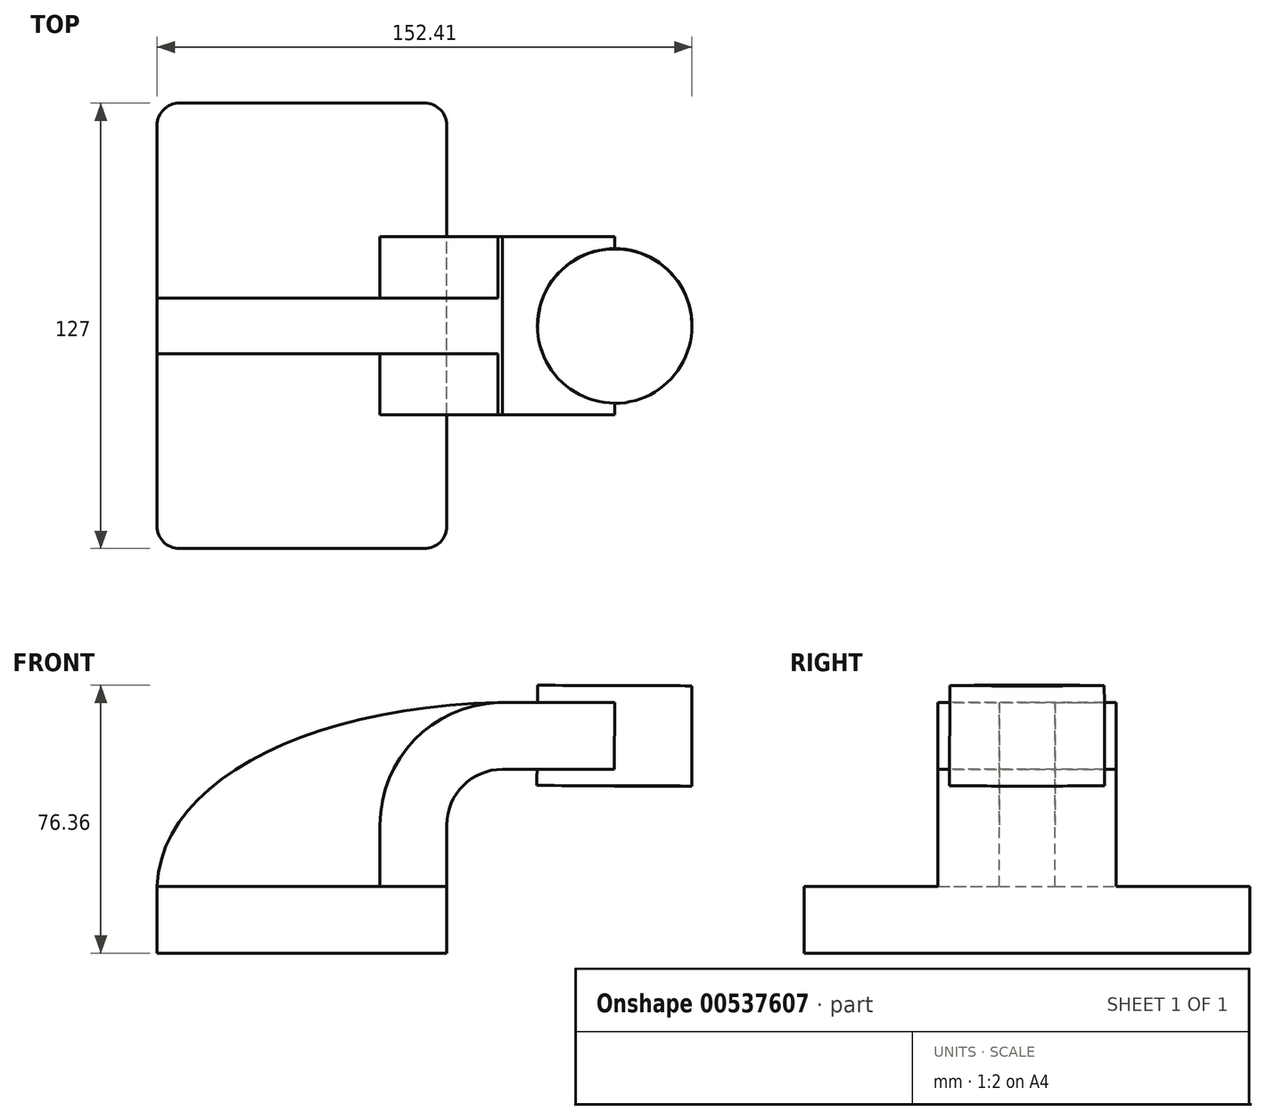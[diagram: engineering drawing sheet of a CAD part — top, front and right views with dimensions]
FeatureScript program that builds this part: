
annotation { "Feature Type Name" : "Feature", "Feature Type Description" : "" }
export const myFeature = defineFeature(function(context is Context, id is Id, definition is map)
    precondition{}
    {
        {
            var Q0;
            Q0=qCreatedBy(makeId("Front.planeOp"),FACE);
            var sketch = newSketch(context, id + "F0", { "sketchPlane" : qUnion([Q0])});
            skLineSegment(sketch, "E0.bottom", {"start": v(-41.28, -9.53) * mm, "end": v(41.28, -9.53) * mm});
            skLineSegment(sketch, "E0.top", {"start": v(-41.28, 9.53) * mm, "end": v(41.28, 9.53) * mm});
            skLineSegment(sketch, "E0.left", {"start": v(-41.28, -9.53) * mm, "end": v(-41.28, 9.53) * mm});
            skLineSegment(sketch, "E0.right", {"start": v(41.28, -9.53) * mm, "end": v(41.28, 9.53) * mm});
            skPoint(sketch, "E0.middle", {"position": v(0, 0) * mm});
            skLineSegment(sketch, "E1.bottom", {"start": v(60.32, 38.1) * mm, "end": v(111.12, 38.1) * mm});
            skLineSegment(sketch, "E1.top", {"start": v(60.32, 66.68) * mm, "end": v(111.12, 66.68) * mm});
            skLineSegment(sketch, "E1.left", {"start": v(60.32, 38.1) * mm, "end": v(60.32, 66.68) * mm});
            skLineSegment(sketch, "E1.right", {"start": v(111.12, 38.1) * mm, "end": v(111.12, 66.68) * mm});
            skPoint(sketch, "E1.middle", {"position": v(85.72, 52.39) * mm});
            skLineSegment(sketch, "E2", {"start": v(41.27, 9.53) * mm, "end": v(41.27, 27) * mm});
            skArc(sketch, "E3", {"start": v(41.27, 27) * mm, "mid": v(45.92, 38.23) * mm, "end": v(57.15, 42.88) * mm});
            skLineSegment(sketch, "E4", {"start": v(57.15, 42.88) * mm, "end": v(89.13, 42.88) * mm});
            skLineSegment(sketch, "E5.0", {"start": v(57.15, 61.93) * mm, "end": v(89.13, 61.93) * mm});
            skArc(sketch, "E5.1", {"start": v(22.23, 27) * mm, "mid": v(32.45, 51.7) * mm, "end": v(57.15, 61.93) * mm});
            skLineSegment(sketch, "E5.2", {"start": v(22.22, 9.53) * mm, "end": v(22.22, 27) * mm});
            skFitSpline(sketch, "E6", {"points": [v(-41.28, 9.53) * mm, v(57.15, 61.93) * mm], "startDerivative": vector(2.95, 90.72) * mm, "endDerivative": vector(163.21, 2.57) * mm});
            skLineSegment(sketch, "E7", {"start": v(89.03, 38.1) * mm, "end": v(89.13, 66.68) * mm});
            skSolve(sketch);
        }
        {
            var Q0;
            Q0=makeQuery(id+"F0.imprint","IMPRINT",FACE,{"disambiguationData":[TD([[makeQuery(id+"F0.imprint","IMPRINT",EDGE,{"derivedFrom":sQuery(id+"F0.wireOp",EDGE,"E0.bottom")}),1.0]])]});
            extrude(context, id + "F1", {"entities" : qUnion([Q0]), "endBound" : BoundingType.SYMMETRIC, "depth" : 127 * mm, "offsetDistance" : 25.4 * mm});
        }
        {
            var Q0;
            {var subQ1=sQuery(id+"F0.wireOp",EDGE,"E2");Q0=makeQuery(id+"F0.imprint","IMPRINT",FACE,{"disambiguationData":[TD([[makeQuery(id+"F0.imprint","IMPRINT",EDGE,{"derivedFrom":subQ1}),1.0]])]});}
            var Q1;
            {var subQ0=sQuery(id+"F0.wireOp",EDGE,"E4");var subQ1=sQuery(id+"F0.wireOp",EDGE,"E1.left");var subQ2=makeQuery(id+"F0.imprint","INTERSECT",VERTEX,{"derivedFrom":[subQ1,subQ0]});Q1=makeQuery(id+"F0.imprint","IMPRINT",FACE,{"disambiguationData":[TD([[makeQuery(id+"F0.imprint","IMPRINT",EDGE,{"disambiguationData":[TD([[subQ2,-1.0]])],"derivedFrom":subQ1}),-1.0]])]});}
            extrude(context, id + "F2", {"entities" : qUnion([Q0, Q1]), "operationType" : NewBodyOperationType.ADD, "endBound" : BoundingType.SYMMETRIC, "depth" : 50.8 * mm, "offsetDistance" : 25.4 * mm});
        }
        {
            var Q0;
            {var subQ3=sQuery(id+"F0.wireOp",EDGE,"E5.2");Q0=makeQuery(id+"F0.imprint","IMPRINT",FACE,{"disambiguationData":[TD([[makeQuery(id+"F0.imprint","IMPRINT",EDGE,{"derivedFrom":subQ3}),1.0]])]});}
            extrude(context, id + "F3", {"entities" : qUnion([Q0]), "operationType" : NewBodyOperationType.ADD, "endBound" : BoundingType.SYMMETRIC, "depth" : 15.88 * mm, "offsetDistance" : 25.4 * mm});
        }
        {
            var Q0;
            {var subQ4=sQuery(id+"F0.wireOp",EDGE,"E1.right");Q0=makeQuery(id+"F0.imprint","IMPRINT",FACE,{"disambiguationData":[TD([[makeQuery(id+"F0.imprint","IMPRINT",EDGE,{"derivedFrom":subQ4}),1.0]])]});}
            var Q1;
            Q1=sQuery(id+"F0.wireOp",EDGE,"E7");
            revolve(context, id + "F4", {"operationType" : NewBodyOperationType.ADD, "entities" : qUnion([Q0]), "axis" : qUnion([Q1]), "revolveType" : RevolveType.FULL});
        }
        {
            var Q0;
            Q0=makeQuery(id+"F1.opExtrude","CAP_EDGE",EDGE,{"disambiguationData":[OSD([sQuery(id+"F0.wireOp",EDGE,"E0.right")])],"isStart":false});
            var Q1;
            Q1=makeQuery(id+"F1.opExtrude","CAP_EDGE",EDGE,{"disambiguationData":[OSD([sQuery(id+"F0.wireOp",EDGE,"E0.left")])],"isStart":false});
            var Q2;
            Q2=makeQuery(id+"F1.opExtrude","CAP_EDGE",EDGE,{"disambiguationData":[OSD([sQuery(id+"F0.wireOp",EDGE,"E0.right")])],"isStart":true});
            var Q3;
            Q3=makeQuery(id+"F1.opExtrude","CAP_EDGE",EDGE,{"disambiguationData":[OSD([sQuery(id+"F0.wireOp",EDGE,"E0.left")])],"isStart":true});
            fillet(context, id + "F5", {"entities" : qUnion([Q0, Q1, Q2, Q3]), "radius" : 6.35 * mm, "tangentPropagation" : true, "allowEdgeOverflow" : false});
        }
    });
